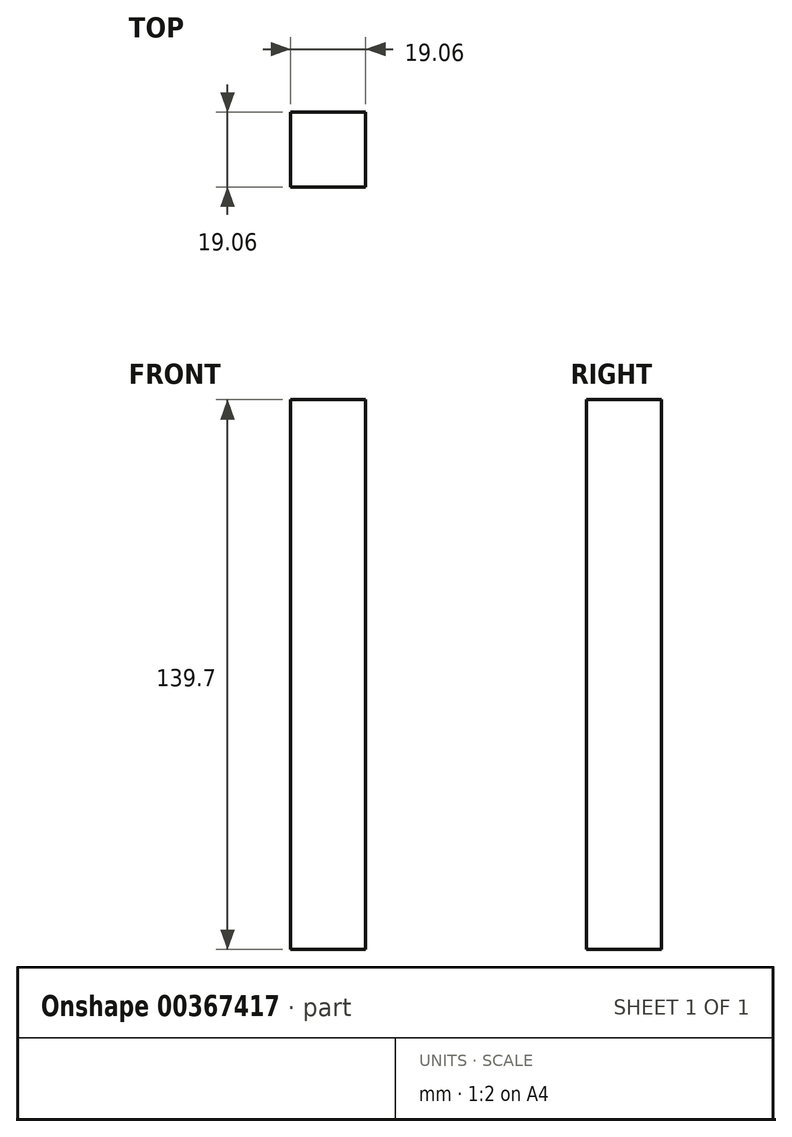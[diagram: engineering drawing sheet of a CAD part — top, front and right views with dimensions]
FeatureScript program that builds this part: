
annotation { "Feature Type Name" : "Feature", "Feature Type Description" : "" }
export const myFeature = defineFeature(function(context is Context, id is Id, definition is map)
    precondition{}
    {
        {
            var Q0;
            Q0=qCreatedBy(makeId("Top.planeOp"),FACE);
            var sketch = newSketch(context, id + "F0", { "sketchPlane" : qUnion([Q0])});
            skLineSegment(sketch, "E0.bottom", {"start": v(9.52, 9.53) * mm, "end": v(-9.53, 9.53) * mm});
            skLineSegment(sketch, "E0.top", {"start": v(9.53, -9.53) * mm, "end": v(-9.52, -9.53) * mm});
            skLineSegment(sketch, "E0.left", {"start": v(9.52, 9.53) * mm, "end": v(9.53, -9.53) * mm});
            skLineSegment(sketch, "E0.right", {"start": v(-9.53, 9.53) * mm, "end": v(-9.52, -9.53) * mm});
            skPoint(sketch, "E0.middle", {"position": v(0, 0) * mm});
            skSolve(sketch);
        }
        {
            var Q0;
            Q0 = qSketchRegion(id + "F0", true);
            extrude(context, id + "F1", {"entities" : qUnion([Q0]), "depth" : 139.7 * mm});
        }
    });
